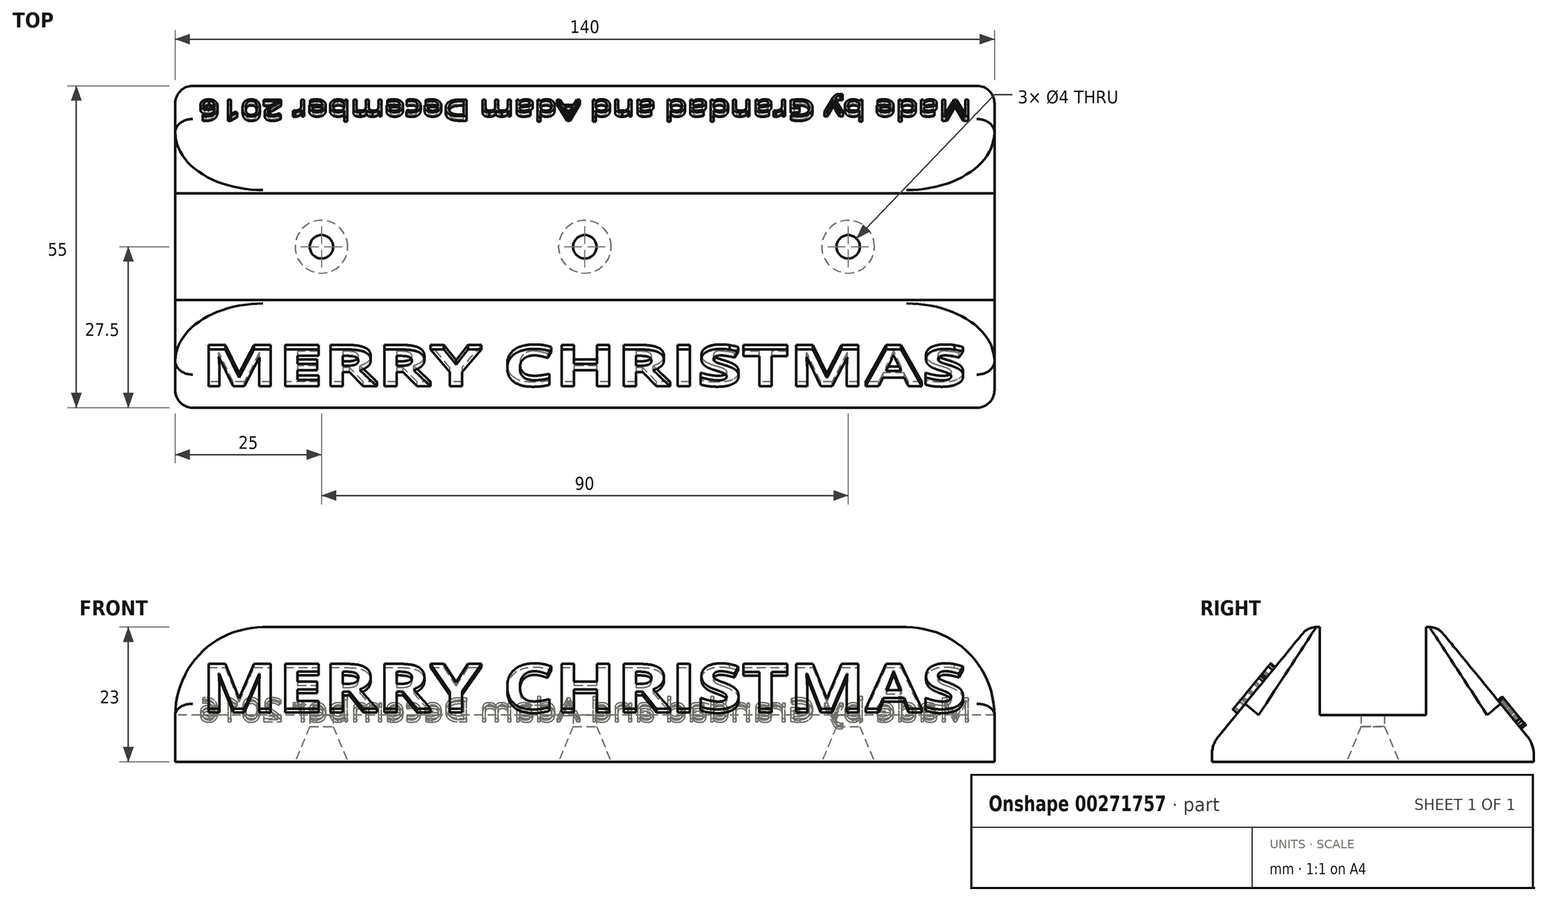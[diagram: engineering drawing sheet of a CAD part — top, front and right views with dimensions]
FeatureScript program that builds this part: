
annotation { "Feature Type Name" : "Feature", "Feature Type Description" : "" }
export const myFeature = defineFeature(function(context is Context, id is Id, definition is map)
    precondition{}
    {
        {
            var Q0;
            Q0=qCreatedBy(makeId("Top.planeOp"),FACE);
            var sketch = newSketch(context, id + "F0", { "sketchPlane" : qUnion([Q0])});
            skLineSegment(sketch, "E0.bottom", {"start": v(-70, 27.5) * mm, "end": v(70, 27.5) * mm});
            skLineSegment(sketch, "E0.top", {"start": v(-70, -27.5) * mm, "end": v(70, -27.5) * mm});
            skLineSegment(sketch, "E0.left", {"start": v(-70, 27.5) * mm, "end": v(-70, -27.5) * mm});
            skLineSegment(sketch, "E0.right", {"start": v(70, 27.5) * mm, "end": v(70, -27.5) * mm});
            skSolve(sketch);
        }
        {
            var Q0;
            Q0 = qSketchRegion(id + "F0", true);
            extrude(context, id + "F1", {"entities" : qUnion([Q0]), "depth" : 3 * mm});
        }
        {
            var Q0;
            Q0=makeQuery(id+"F1.opExtrude","SWEPT_FACE",FACE,{"disambiguationData":[OSD([sQuery(id+"F0.wireOp",EDGE,"E0.left")])]});
            var sketch = newSketch(context, id + "F2", { "sketchPlane" : qUnion([Q0])});
            skLineSegment(sketch, "E1", {"start": v(27.5, 3) * mm, "end": v(27.5, 0) * mm});
            skLineSegment(sketch, "E2", {"start": v(27.5, 0) * mm, "end": v(-27.5, 0) * mm});
            skLineSegment(sketch, "E3", {"start": v(-27.5, 0) * mm, "end": v(-27.5, 3) * mm});
            skLineSegment(sketch, "E4", {"start": v(-27.5, 3) * mm, "end": v(-11.1, 23) * mm});
            skLineSegment(sketch, "E5", {"start": v(-11.1, 23) * mm, "end": v(-9.1, 23) * mm});
            skLineSegment(sketch, "E6", {"start": v(-9.1, 23) * mm, "end": v(-9.1, 8) * mm});
            skLineSegment(sketch, "E7", {"start": v(-9.1, 8) * mm, "end": v(9.1, 8) * mm});
            skLineSegment(sketch, "E8", {"start": v(9.1, 8) * mm, "end": v(9.1, 23) * mm});
            skLineSegment(sketch, "E9", {"start": v(9.1, 23) * mm, "end": v(11.1, 23) * mm});
            skLineSegment(sketch, "E10", {"start": v(11.1, 23) * mm, "end": v(27.5, 3) * mm});
            skSolve(sketch);
        }
        {
            var Q0;
            Q0 = qSketchRegion(id + "F2", true);
            extrude(context, id + "F3", {"entities" : qUnion([Q0]), "operationType" : NewBodyOperationType.ADD, "oppositeDirection" : true, "depth" : 140 * mm});
        }
        {
            var Q0;
            Q0=makeQuery(id+"F3.opExtrude","CAP_EDGE",EDGE,{"disambiguationData":[OSD([sQuery(id+"F2.wireOp",EDGE,"E9")])],"isStart":true});
            var Q1;
            Q1=makeQuery(id+"F3.opExtrude","CAP_EDGE",EDGE,{"disambiguationData":[OSD([sQuery(id+"F2.wireOp",EDGE,"E5")])],"isStart":true});
            var Q2;
            Q2=makeQuery(id+"F3.opExtrude","CAP_EDGE",EDGE,{"disambiguationData":[OSD([sQuery(id+"F2.wireOp",EDGE,"E5")])],"isStart":false});
            var Q3;
            Q3=makeQuery(id+"F3.opExtrude","CAP_EDGE",EDGE,{"disambiguationData":[OSD([sQuery(id+"F2.wireOp",EDGE,"E9")])],"isStart":false});
            fillet(context, id + "F4", {"entities" : qUnion([Q0, Q1, Q2, Q3]), "radius" : 15 * mm, "tangentPropagation" : true, "allowEdgeOverflow" : false});
        }
        {
            var Q0;
            Q0=makeQuery(id+"F3.opExtrude","SWEPT_FACE",FACE,{"disambiguationData":[OSD([sQuery(id+"F2.wireOp",EDGE,"E10")])]});
            var sketch = newSketch(context, id + "F5", { "sketchPlane" : qUnion([Q0])});
            skText(sketch, "E11", { "text": "MERRY CHRISTMAS", "fontName": "OpenSans-Bold.ttf"});
            const initialGuessF5  = {"E11": [-0.06555, -0.00812, 1, 0, 0.01]};
            skSetInitialGuess(sketch, initialGuessF5);
            skSolve(sketch);
        }
        {
            var Q0;
            Q0 = qSketchRegion(id + "F5", true);
            extrude(context, id + "F6", {"entities" : qUnion([Q0]), "operationType" : NewBodyOperationType.ADD, "depth" : 1 * mm});
        }
        {
            var Q0;
            Q0=makeQuery(id+"F3.boolean.opBoolean","MERGE",EDGE,{"derivedFrom":[makeQuery(id+"F1.opExtrude","CAP_EDGE",EDGE,{"disambiguationData":[OSD([sQuery(id+"F0.wireOp",EDGE,"E0.top")])],"isStart":false}),makeQuery(id+"F3.opExtrude","SWEPT_EDGE",EDGE,{"disambiguationData":[OSD([sQuery(id+"F0.wireOp",EDGE,"E0.left"),sQuery(id+"F2.wireOp",EDGE,"E1"),sQuery(id+"F2.wireOp",EDGE,"E10")])]})]});
            var Q1;
            Q1=makeQuery(id+"F3.boolean.opBoolean","MERGE",EDGE,{"derivedFrom":[makeQuery(id+"F1.opExtrude","CAP_EDGE",EDGE,{"disambiguationData":[OSD([sQuery(id+"F0.wireOp",EDGE,"E0.bottom")])],"isStart":false}),makeQuery(id+"F3.opExtrude","SWEPT_EDGE",EDGE,{"disambiguationData":[OSD([sQuery(id+"F0.wireOp",EDGE,"E0.left"),sQuery(id+"F2.wireOp",EDGE,"E3"),sQuery(id+"F2.wireOp",EDGE,"E4")])]})]});
            fillet(context, id + "F7", {"entities" : qUnion([Q0, Q1]), "radius" : 5 * mm, "tangentPropagation" : true, "allowEdgeOverflow" : false});
        }
        {
            var Q0;
            Q0=makeQuery(id+"F4.opFillet","BLEND_EDGE",EDGE,{"blendedFrom":[makeQuery(id+"F3.opExtrude","CAP_EDGE",EDGE,{"disambiguationData":[OSD([sQuery(id+"F2.wireOp",EDGE,"E9")])],"isStart":true}),makeQuery(id+"F3.opExtrude","SWEPT_FACE",FACE,{"disambiguationData":[OSD([sQuery(id+"F2.wireOp",EDGE,"E10")])]})],"blendedInto":[makeQuery(id+"F3.opExtrude","SWEPT_FACE",FACE,{"disambiguationData":[OSD([sQuery(id+"F2.wireOp",EDGE,"E10")])]})]});
            var Q1;
            Q1=makeQuery(id+"F4.opFillet","BLEND_EDGE",EDGE,{"blendedFrom":[makeQuery(id+"F3.opExtrude","CAP_EDGE",EDGE,{"disambiguationData":[OSD([sQuery(id+"F2.wireOp",EDGE,"E5")])],"isStart":true}),makeQuery(id+"F3.opExtrude","SWEPT_FACE",FACE,{"disambiguationData":[OSD([sQuery(id+"F2.wireOp",EDGE,"E4")])]})],"blendedInto":[makeQuery(id+"F3.opExtrude","SWEPT_FACE",FACE,{"disambiguationData":[OSD([sQuery(id+"F2.wireOp",EDGE,"E4")])]})]});
            fillet(context, id + "F8", {"entities" : qUnion([Q0, Q1]), "radius" : 3 * mm, "tangentPropagation" : true, "allowEdgeOverflow" : false});
        }
        {
            var Q0;
            Q0=makeQuery(id+"F1.opExtrude","CAP_FACE",FACE,{"disambiguationData":[OSD([sQuery(id+"F0.wireOp",EDGE,"E0.bottom"),sQuery(id+"F0.wireOp",EDGE,"E0.top"),sQuery(id+"F0.wireOp",EDGE,"E0.left"),sQuery(id+"F0.wireOp",EDGE,"E0.right")])],"isStart":true});
            var sketch = newSketch(context, id + "F9", { "sketchPlane" : qUnion([Q0])});
            skPoint(sketch, "E12", {"position": v(0, 0) * mm});
            skPoint(sketch, "E13", {"position": v(-45, 0) * mm});
            skPoint(sketch, "E14", {"position": v(45, 0) * mm});
            skSolve(sketch);
        }
        {
            var Q0;
            Q0=sQuery(id+"F9.wireOp",VERTEX,"E13");
            var Q1;
            Q1=sQuery(id+"F9.wireOp",VERTEX,"E12");
            var Q2;
            Q2=sQuery(id+"F9.wireOp",VERTEX,"E14");
            var Q3;
            Q3=makeQuery(id+"F1.opExtrude","SWEPT_BODY",BODY,{"disambiguationData":[OSD([sQuery(id+"F0.wireOp",EDGE,"E0.bottom"),sQuery(id+"F0.wireOp",EDGE,"E0.top"),sQuery(id+"F0.wireOp",EDGE,"E0.left"),sQuery(id+"F0.wireOp",EDGE,"E0.right")])]});
            hole(context, id + "F10", {"style" : HoleStyle.C_SINK, "endStyle" : HoleEndStyle.BLIND, "holeDiameter" : 4 * mm, "cSinkDiameter" : 9 * mm, "cSinkAngle" : 45 * degree, "holeDepth" : 15 * mm, "isTappedThrough" : true, "tappedDepth" : 12 * mm, "tapClearance" : 3, "startFromSketch" : true, "locations" : qUnion([Q0, Q1, Q2]), "scope" : qUnion([Q3])});
        }
        {
            var Q0;
            Q0=makeQuery(id+"F3.opExtrude","SWEPT_FACE",FACE,{"disambiguationData":[OSD([sQuery(id+"F2.wireOp",EDGE,"E4")])]});
            var sketch = newSketch(context, id + "F11", { "sketchPlane" : qUnion([Q0])});
            skText(sketch, "E15", { "text": "Made by Grandad and Adam December 2016", "fontName": "OpenSans-Regular.ttf"});
            const initialGuessF11  = {"E15": [-0.0661, -0.0102, 1, 0, 0.00452]};
            skSetInitialGuess(sketch, initialGuessF11);
            skSolve(sketch);
        }
        {
            var Q0;
            Q0 = qSketchRegion(id + "F11", true);
            extrude(context, id + "F12", {"entities" : qUnion([Q0]), "operationType" : NewBodyOperationType.ADD, "depth" : 1 * mm});
        }
    });
